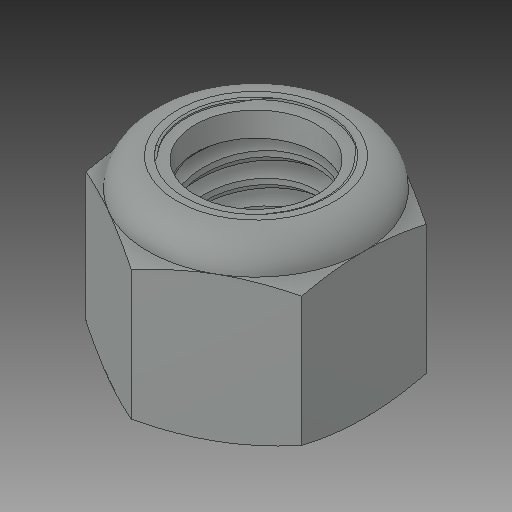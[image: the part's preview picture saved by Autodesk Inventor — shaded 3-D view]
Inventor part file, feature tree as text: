
AUTODESK INVENTOR PART (.ipt)
format: ipt  version: 2018 (Build 220112000, 112)  size: 344,064 bytes
history: native  units: in
note: dims shown in document units (in); Inventor stores cm internally (conversion verified against a paired STEP export)
features: other x1, revolve x1
ambient origin geometry x8: Origin, YZ Plane, XZ Plane, XY Plane, X Axis, Y Axis, Z Axis, Center Point
bodies: Solid1 (feature_tree), Solid2 (feature_tree)
feature tree (2):
  other  "Cut-Revolve4"
  revolve  "Revolve2"  [1 undecoded]
note: 1 required parameter value undecoded (feature->parameter linkage not recoverable at this tier; creation-order binding heuristic only, values carry confidence <= 0.55)
